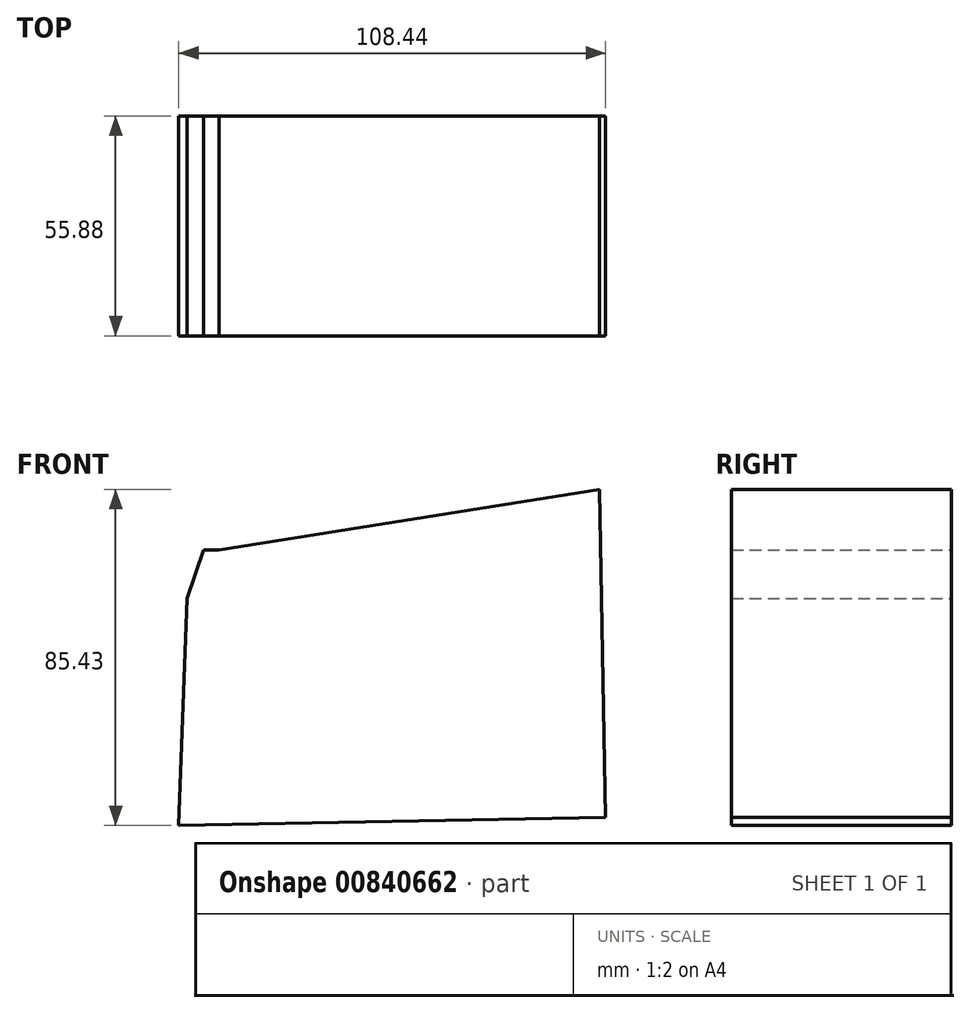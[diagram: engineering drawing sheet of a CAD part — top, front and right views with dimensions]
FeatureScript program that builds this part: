
annotation { "Feature Type Name" : "Feature", "Feature Type Description" : "" }
export const myFeature = defineFeature(function(context is Context, id is Id, definition is map)
    precondition{}
    {
        {
            var Q0;
            Q0=qCreatedBy(makeId("Front.planeOp"),FACE);
            var sketch = newSketch(context, id + "F0", { "sketchPlane" : qUnion([Q0])});
            skLineSegment(sketch, "E0", {"start": v(-45.6, 34.8) * mm, "end": v(-41.62, 34.8) * mm});
            skLineSegment(sketch, "E1", {"start": v(-49.77, 22.47) * mm, "end": v(-51.85, -35.36) * mm});
            skLineSegment(sketch, "E2", {"start": v(-55.08, -35.36) * mm, "end": v(56.6, -33.27) * mm});
            skLineSegment(sketch, "E3", {"start": v(56.6, -33.27) * mm, "end": v(55.04, 50.13) * mm});
            skLineSegment(sketch, "E4", {"start": v(55.04, 50.13) * mm, "end": v(-41.62, 34.8) * mm});
            skLineSegment(sketch, "E5", {"start": v(-49.77, 22.47) * mm, "end": v(-45.6, 34.8) * mm});
            skSolve(sketch);
        }
        {
            var Q0;
            Q0=makeQuery(id+"F0.imprint","IMPRINT",FACE,{"disambiguationData":[TD([[makeQuery(id+"F0.imprint","IMPRINT",EDGE,{"derivedFrom":sQuery(id+"F0.wireOp",EDGE,"E0")}),-1.0]])]});
            extrude(context, id + "F1", {"entities" : qUnion([Q0]), "depth" : 55.88 * mm, "offsetDistance" : 25.4 * mm});
        }
    });
